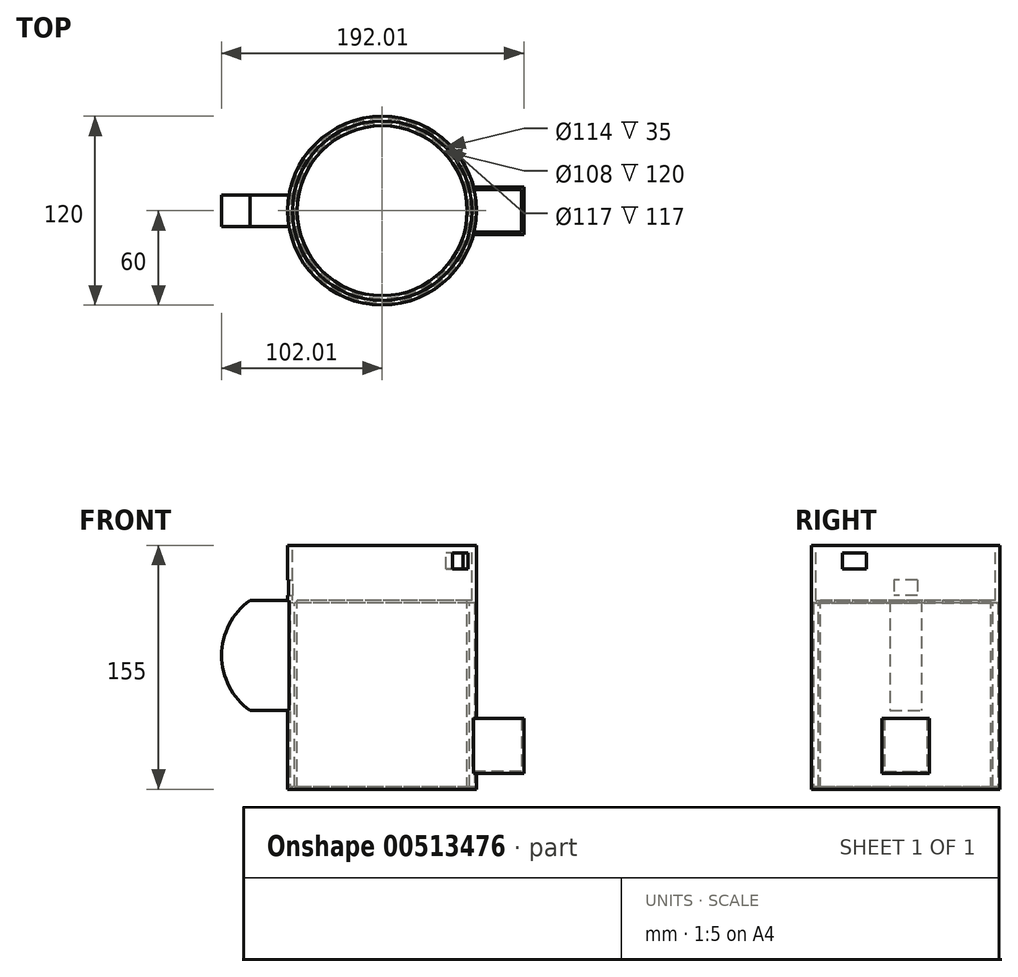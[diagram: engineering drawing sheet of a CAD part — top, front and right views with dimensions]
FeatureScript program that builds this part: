
annotation { "Feature Type Name" : "Feature", "Feature Type Description" : "" }
export const myFeature = defineFeature(function(context is Context, id is Id, definition is map)
    precondition{}
    {
        {
            var Q0;
            Q0=qCreatedBy(makeId("Top.planeOp"),FACE);
            var sketch = newSketch(context, id + "F0", { "sketchPlane" : qUnion([Q0])});
            skCircle(sketch, "E0", {"center": v(0, 0) * mm, "radius": 60 * mm});
            skSolve(sketch);
        }
        {
            var Q0;
            Q0=makeQuery(id+"F0.imprint","IMPRINT",FACE,{"disambiguationData":[TD([[makeQuery(id+"F0.imprint","IMPRINT",EDGE,{"derivedFrom":sQuery(id+"F0.wireOp",EDGE,"E0")}),1.0]])]});
            extrude(context, id + "F1", {"entities" : qUnion([Q0]), "depth" : 155 * mm, "offsetDistance" : 25 * mm});
        }
        {
            var Q0;
            Q0=makeQuery(id+"F1.opExtrude","CAP_FACE",FACE,{"disambiguationData":[OSD([sQuery(id+"F0.wireOp",EDGE,"E0")])],"isStart":false});
            var sketch = newSketch(context, id + "F2", { "sketchPlane" : qUnion([Q0])});
            skCircle(sketch, "E1", {"center": v(0, 0) * mm, "radius": 54 * mm});
            skSolve(sketch);
        }
        {
            var Q0;
            Q0=makeQuery(id+"F2.imprint","IMPRINT",FACE,{"disambiguationData":[TD([[makeQuery(id+"F2.imprint","IMPRINT",EDGE,{"derivedFrom":sQuery(id+"F2.wireOp",EDGE,"E1")}),1.0]])]});
            var Q1;
            Q1 = qSketchRegion(id + "F0", true);
            extrude(context, id + "F3", {"entities" : qUnion([Q0, Q1]), "operationType" : NewBodyOperationType.REMOVE, "oppositeDirection" : true, "depth" : 190 * mm, "offsetDistance" : 25 * mm});
        }
        {
            var Q0;
            Q0=makeQuery(id+"F1.opExtrude","CAP_FACE",FACE,{"disambiguationData":[OSD([sQuery(id+"F0.wireOp",EDGE,"E0")])],"isStart":false});
            var sketch = newSketch(context, id + "F4", { "sketchPlane" : qUnion([Q0])});
            skCircle(sketch, "E2", {"center": v(0, 0) * mm, "radius": 57 * mm});
            skSolve(sketch);
        }
        {
            var Q0;
            Q0=makeQuery(id+"F4.imprint","IMPRINT",FACE,{"disambiguationData":[TD([[makeQuery(id+"F4.imprint","IMPRINT",EDGE,{"derivedFrom":makeQuery(id+"F3.boolean.opBoolean","COPY",EDGE,{"derivedFrom":makeQuery(id+"F3.opExtrude","CAP_EDGE",EDGE,{"disambiguationData":[OSD([sQuery(id+"F2.wireOp",EDGE,"E1")])],"isStart":true})})}),1.0]])]});
            var Q1;
            Q1=makeQuery(id+"F4.imprint","IMPRINT",FACE,{"disambiguationData":[TD([[makeQuery(id+"F4.imprint","IMPRINT",EDGE,{"derivedFrom":sQuery(id+"F4.wireOp",EDGE,"E2")}),1.0]])]});
            extrude(context, id + "F5", {"entities" : qUnion([Q0, Q1]), "operationType" : NewBodyOperationType.REMOVE, "oppositeDirection" : true, "depth" : 35 * mm, "offsetDistance" : 25 * mm});
        }
        {
            var Q0;
            Q0=qCreatedBy(makeId("Top.planeOp"),FACE);
            cPlane(context, id + "F6", {"entities" : qUnion([Q0]), "cplaneType" : CPlaneType.OFFSET, "offset" : 10 * mm, "width" : 150 * mm, "height" : 150 * mm});
        }
        {
            var Q0;
            Q0=qCreatedBy(id+"F6.planeOp",FACE);
            var sketch = newSketch(context, id + "F7", { "sketchPlane" : qUnion([Q0])});
            skPoint(sketch, "E3", {"position": v(0, 0) * mm});
            skLineSegment(sketch, "E4", {"start": v(0, 0) * mm, "end": v(60, 0) * mm});
            skLineSegment(sketch, "E5", {"start": v(60, 0) * mm, "end": v(90, 0) * mm});
            skLineSegment(sketch, "E6", {"start": v(90, 0) * mm, "end": v(90, 15) * mm});
            skLineSegment(sketch, "E7", {"start": v(90, 0) * mm, "end": v(90, -15) * mm});
            skLineSegment(sketch, "E8", {"start": v(90, -15) * mm, "end": v(0, -15) * mm});
            skLineSegment(sketch, "E9", {"start": v(90, 15) * mm, "end": v(0, 15) * mm});
            skCircle(sketch, "E10", {"center": v(0, 0) * mm, "radius": 60 * mm});
            skSolve(sketch);
        }
        {
            var Q0;
            {var subQ0=sQuery(id+"F7.wireOp",EDGE,"E5");Q0=makeQuery(id+"F7.imprint","IMPRINT",FACE,{"disambiguationData":[TD([[makeQuery(id+"F7.imprint","IMPRINT",EDGE,{"derivedFrom":subQ0}),1.0]])]});}
            var Q1;
            {var subQ0=sQuery(id+"F7.wireOp",EDGE,"E5");Q1=makeQuery(id+"F7.imprint","IMPRINT",FACE,{"disambiguationData":[TD([[makeQuery(id+"F7.imprint","IMPRINT",EDGE,{"derivedFrom":subQ0}),-1.0]])]});}
            extrude(context, id + "F8", {"entities" : qUnion([Q0, Q1]), "operationType" : NewBodyOperationType.ADD, "depth" : 35 * mm, "offsetDistance" : 25 * mm});
        }
        {
            var Q0;
            Q0=makeQuery(id+"F8.opExtrude","CAP_FACE",FACE,{"disambiguationData":[OSD([sQuery(id+"F7.wireOp",EDGE,"E6"),sQuery(id+"F7.wireOp",EDGE,"E7"),sQuery(id+"F7.wireOp",EDGE,"E8"),sQuery(id+"F7.wireOp",EDGE,"E9"),sQuery(id+"F7.wireOp",EDGE,"E10")])],"isStart":false});
            shell(context, id + "F9", {"entities" : qUnion([Q0]), "thickness" : 1.5 * mm});
        }
        {
            var Q0;
            Q0=qCreatedBy(makeId("Front.planeOp"),FACE);
            var sketch = newSketch(context, id + "F10", { "sketchPlane" : qUnion([Q0])});
            skLineSegment(sketch, "E11", {"start": v(0, 0) * mm, "end": v(0, 85) * mm, "construction": true});
            skLineSegment(sketch, "E12", {"start": v(0, 85) * mm, "end": v(-59, 85) * mm, "construction": true});
            skLineSegment(sketch, "E13", {"start": v(-59, 85) * mm, "end": v(-59, 135) * mm});
            skLineSegment(sketch, "E14", {"start": v(-59, 85) * mm, "end": v(-59, 35) * mm});
            skLineSegment(sketch, "E15", {"start": v(-59, 135) * mm, "end": v(-84, 135) * mm});
            skLineSegment(sketch, "E16", {"start": v(-59, 35) * mm, "end": v(-84, 35) * mm});
            skArc(sketch, "E17", {"start": v(-84, 135) * mm, "mid": v(-114.9, 85) * mm, "end": v(-84, 35) * mm});
            skLineSegment(sketch, "E18", {"start": v(-59, 85) * mm, "end": v(-59, 120) * mm});
            skLineSegment(sketch, "E19", {"start": v(-59, 85) * mm, "end": v(-59, 60) * mm});
            skLineSegment(sketch, "E20", {"start": v(-59, 120) * mm, "end": v(-84, 120) * mm});
            skLineSegment(sketch, "E21", {"start": v(-59, 85) * mm, "end": v(-59, 50) * mm, "construction": true});
            skLineSegment(sketch, "E22", {"start": v(-59, 50) * mm, "end": v(-84, 50) * mm});
            skArc(sketch, "E23", {"start": v(-84, 120) * mm, "mid": v(-102.01, 85) * mm, "end": v(-84, 50) * mm});
            skSolve(sketch);
        }
        {
            var Q0;
            Q0=makeQuery(id+"F10.imprint","IMPRINT",FACE,{"disambiguationData":[TD([[makeQuery(id+"F10.imprint","IMPRINT",EDGE,{"derivedFrom":sQuery(id+"F10.wireOp",EDGE,"E13")}),1.0]])]});
            extrude(context, id + "F11", {"entities" : qUnion([Q0]), "operationType" : NewBodyOperationType.ADD, "depth" : 10 * mm, "offsetDistance" : 25 * mm, "hasSecondDirection" : true, "secondDirectionOppositeDirection" : true, "secondDirectionDepth" : 10 * mm});
        }
        {
            var Q0;
            Q0=qCreatedBy(makeId("Right.planeOp"),FACE);
            var sketch = newSketch(context, id + "F12", { "sketchPlane" : qUnion([Q0])});
            skLineSegment(sketch, "E24", {"start": v(0, 0) * mm, "end": v(0, 150) * mm, "construction": true});
            skLineSegment(sketch, "E25", {"start": v(0, 150) * mm, "end": v(-25, 150) * mm, "construction": true});
            skLineSegment(sketch, "E26", {"start": v(-25, 150) * mm, "end": v(-40, 150) * mm});
            skLineSegment(sketch, "E27", {"start": v(-40, 150) * mm, "end": v(-40, 140) * mm});
            skLineSegment(sketch, "E28", {"start": v(-40, 140) * mm, "end": v(-25, 140) * mm});
            skLineSegment(sketch, "E29", {"start": v(-25, 140) * mm, "end": v(-25, 150) * mm});
            skSolve(sketch);
        }
        {
            var Q0;
            Q0=makeQuery(id+"F12.imprint","IMPRINT",FACE,{"disambiguationData":[TD([[makeQuery(id+"F12.imprint","IMPRINT",EDGE,{"derivedFrom":sQuery(id+"F12.wireOp",EDGE,"E26")}),1.0]])]});
            extrude(context, id + "F13", {"entities" : qUnion([Q0]), "operationType" : NewBodyOperationType.REMOVE, "depth" : 74.7 * mm, "offsetDistance" : 25 * mm});
        }
        {
            var Q0;
            Q0=qCreatedBy(makeId("Right.planeOp"),FACE);
            var sketch = newSketch(context, id + "F14", { "sketchPlane" : qUnion([Q0])});
            skLineSegment(sketch, "E30", {"start": v(0, 0) * mm, "end": v(0, 128) * mm, "construction": true});
            skLineSegment(sketch, "E31.bottom", {"start": v(7.5, 133) * mm, "end": v(-7.5, 133) * mm});
            skLineSegment(sketch, "E31.top", {"start": v(7.5, 123) * mm, "end": v(-7.5, 123) * mm});
            skLineSegment(sketch, "E31.left", {"start": v(7.5, 133) * mm, "end": v(7.5, 123) * mm});
            skLineSegment(sketch, "E31.right", {"start": v(-7.5, 133) * mm, "end": v(-7.5, 123) * mm});
            skPoint(sketch, "E31.middle", {"position": v(0, 128) * mm});
            skSolve(sketch);
        }
        {
            var Q0;
            Q0 = qSketchRegion(id + "F14", true);
            extrude(context, id + "F15", {"entities" : qUnion([Q0]), "operationType" : NewBodyOperationType.REMOVE, "oppositeDirection" : true, "depth" : 85.8 * mm, "offsetDistance" : 25 * mm});
        }
        {
            var Q0;
            Q0=qCreatedBy(makeId("Top.planeOp"),FACE);
            cPlane(context, id + "F16", {"entities" : qUnion([Q0]), "cplaneType" : CPlaneType.OFFSET, "offset" : 129 * mm, "width" : 150 * mm, "height" : 150 * mm});
        }
        {
            var Q0;
            Q0=qCreatedBy(id+"F16.planeOp",FACE);
            var sketch = newSketch(context, id + "F17", { "sketchPlane" : qUnion([Q0])});
            skLineSegment(sketch, "E32", {"start": v(0, 0) * mm, "end": v(-73.5, 0) * mm, "construction": true});
            skCircle(sketch, "E33", {"center": v(-73.5, 0) * mm, "radius": 4 * mm});
            skSolve(sketch);
        }
        {
            var Q0;
            Q0=makeQuery(id+"F17.imprint","IMPRINT",FACE,{"disambiguationData":[TD([[makeQuery(id+"F17.imprint","IMPRINT",EDGE,{"derivedFrom":sQuery(id+"F17.wireOp",EDGE,"E33")}),1.0]])]});
            extrude(context, id + "F18", {"entities" : qUnion([Q0]), "operationType" : NewBodyOperationType.REMOVE, "depth" : 20.9 * mm, "offsetDistance" : 25 * mm});
        }
    });
